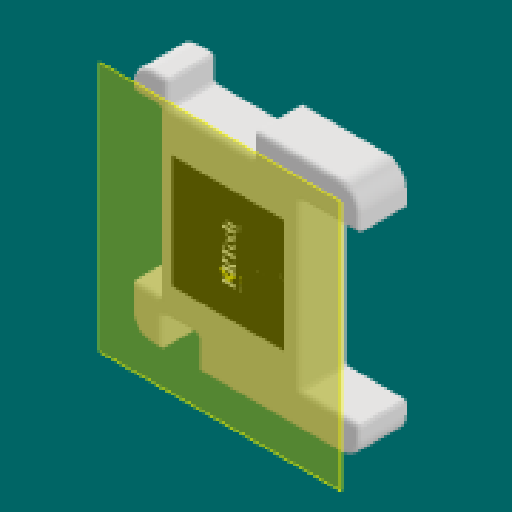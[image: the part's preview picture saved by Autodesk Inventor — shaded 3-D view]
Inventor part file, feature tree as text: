
AUTODESK INVENTOR PART (.ipt)
format: ipt  version: 2025.2 (Build 292293000, 293)  size: 482,304 bytes
history: native  units: mm
features: reference x8, other x6, sketch x3, plane x2, extrude x2, fillet x2
ambient origin geometry x8: Origin, YZ Plane, XZ Plane, XY Plane, X Axis, Y Axis, Z Axis, Center Point
bodies: Solid1 (feature_tree)
feature tree (23):
  plane  "Work Plane1"
  extrude  "Extrusion1"  Depth=9.0mm
  extrude  "Extrusion2"  Depth=1.0mm
  fillet  "Fillet1"  Radius=1.0mm
  fillet  "Fillet2"  Radius=3.0mm
  plane  "Work Plane2"
  other  "Decal3"
  sketch  "Sketch1"  dims[d1=9.0mm d2=9.0mm]
  reference  "Reference1"
  reference  "Reference2"
  reference  "Reference3"
  reference  "Reference4"
  sketch  "Sketch2"  dims[d8=1.0mm d9=1.0mm d10=1.0mm d11=3.0mm]
  reference  "Reference5"
  reference  "Reference6"
  reference  "Reference7"
  reference  "Reference8"
  sketch  "Sketch3"  dims[d13=3.0mm d21=0.5mm d23=0.5mm d25=2.0mm d26=2.05429mm d27=21.085mm d28=0.0mm d33=2.0mm d34=10.0mm d35=0.0mm d36=2.0mm d37=3.0mm d38=16.5mm]
  other  "Image2"
  other  "CASSING_BAS_MEKANIK.iam"
  other  "BAS_Hardware:1"
  other  "Part_atas:1"
  other  "Assembly9"
